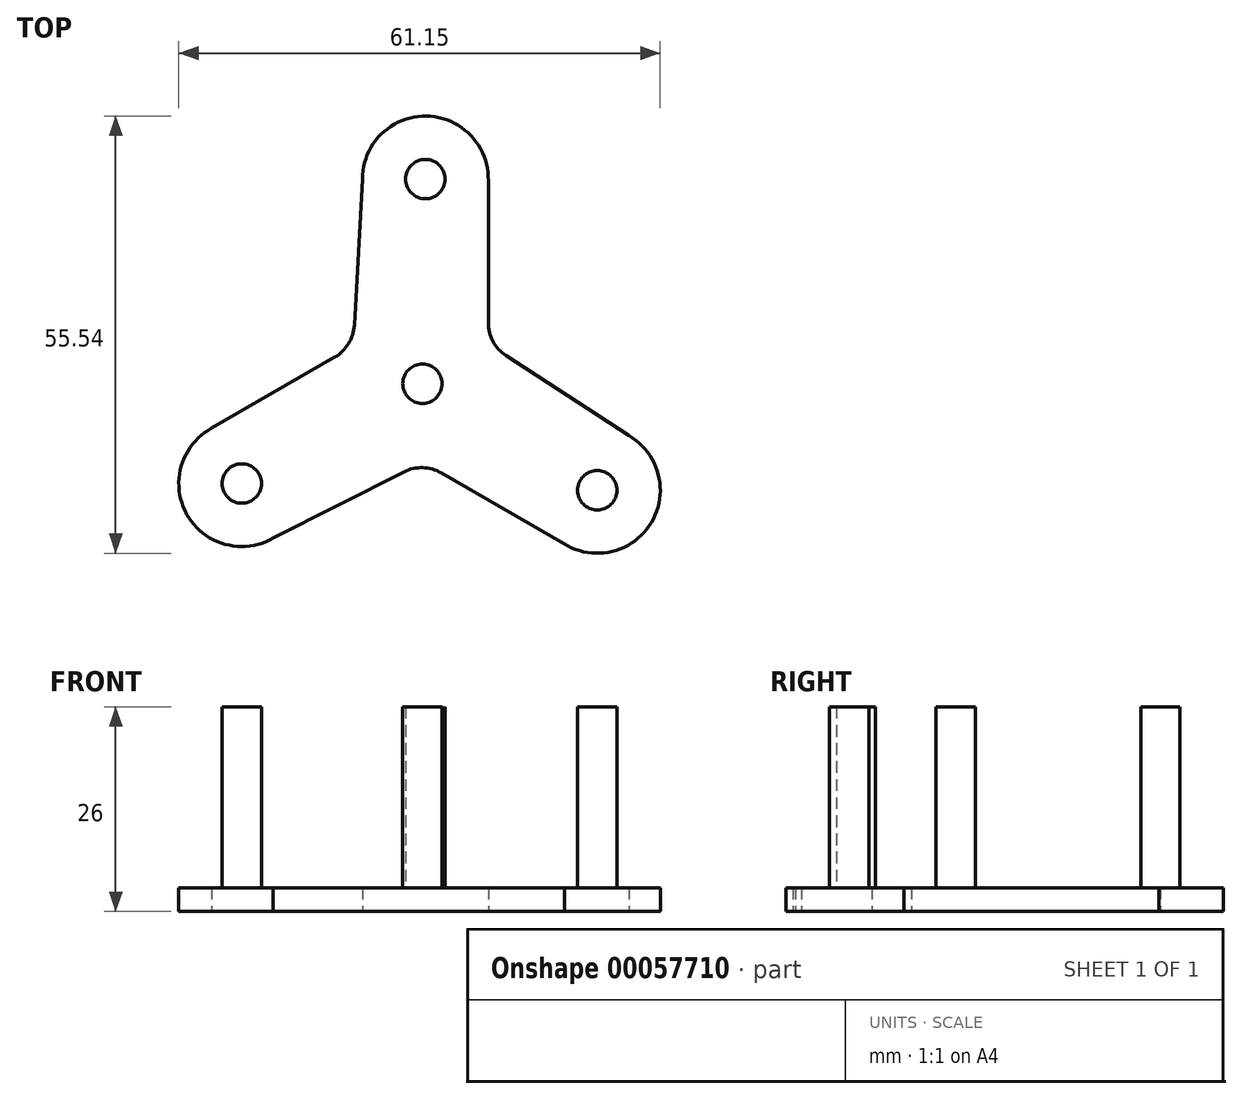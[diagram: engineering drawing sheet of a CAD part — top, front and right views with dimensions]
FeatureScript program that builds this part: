
annotation { "Feature Type Name" : "Feature", "Feature Type Description" : "" }
export const myFeature = defineFeature(function(context is Context, id is Id, definition is map)
    precondition{}
    {
        {
            var Q0;
            Q0=qCreatedBy(makeId("Top.planeOp"),FACE);
            var sketch = newSketch(context, id + "F0", { "sketchPlane" : qUnion([Q0])});
            skCircle(sketch, "E0", {"center": v(0, 0) * mm, "radius": 2.5 * mm});
            skCircle(sketch, "E1", {"center": v(0.37, 26) * mm, "radius": 2.5 * mm});
            skLineSegment(sketch, "E2", {"start": v(0.37, 26) * mm, "end": v(0, 0) * mm});
            skArc(sketch, "E3", {"start": v(8.37, 25.78) * mm, "mid": v(0.48, 34) * mm, "end": v(-7.63, 26) * mm});
            skCircle(sketch, "E4", {"center": v(0, 0) * mm, "radius": 9 * mm});
            skLineSegment(sketch, "E5", {"start": v(-8.65, 7.43) * mm, "end": v(-7.63, 26) * mm});
            skLineSegment(sketch, "E6", {"start": v(8.37, 25.78) * mm, "end": v(8.37, 7.75) * mm});
            skLineSegment(sketch, "E7.1.0", {"start": v(-2.36, -11.2) * mm, "end": v(-18.95, -19.6) * mm});
            skArc(sketch, "E7.1.1", {"start": v(-26.76, -5.65) * mm, "mid": v(-29.93, -16.59) * mm, "end": v(-18.95, -19.6) * mm});
            skLineSegment(sketch, "E7.1.2", {"start": v(-26.76, -5.65) * mm, "end": v(-11.15, 3.37) * mm});
            skCircle(sketch, "E7.1.3", {"center": v(-22.95, -12.68) * mm, "radius": 2.5 * mm});
            skLineSegment(sketch, "E7.1.4", {"start": v(-22.95, -12.68) * mm, "end": v(-0.25, 0) * mm});
            skLineSegment(sketch, "E7.2.0", {"start": v(10.63, 3.56) * mm, "end": v(26.2, -6.6) * mm});
            skArc(sketch, "E7.2.1", {"start": v(18.02, -20.35) * mm, "mid": v(29.08, -17.63) * mm, "end": v(26.2, -6.6) * mm});
            skLineSegment(sketch, "E7.2.2", {"start": v(18.02, -20.35) * mm, "end": v(2.4, -11.34) * mm});
            skCircle(sketch, "E7.2.3", {"center": v(22.2, -13.54) * mm, "radius": 2.5 * mm});
            skLineSegment(sketch, "E7.2.4", {"start": v(22.2, -13.54) * mm, "end": v(-0.13, -0.22) * mm});
            skPoint(sketch, "E7.center", {"position": v(-0.13, -0.07) * mm});
            skPoint(sketch, "E8.newPointA", {"position": v(-4.44, 7.24) * mm});
            skPoint(sketch, "E8.newPointB", {"position": v(-9.06, 0) * mm});
            skArc(sketch, "E8.filletArc", {"start": v(-11.15, 3.37) * mm, "mid": v(-9.39, 5.08) * mm, "end": v(-8.65, 7.43) * mm});
            skArc(sketch, "E9.1.0", {"start": v(2.4, -11.34) * mm, "mid": v(0.04, -10.67) * mm, "end": v(-2.36, -11.2) * mm});
            skArc(sketch, "E9.2.0", {"start": v(8.37, 7.75) * mm, "mid": v(8.97, 5.37) * mm, "end": v(10.63, 3.56) * mm});
            skPoint(sketch, "E10.orphan", {"position": v(8.37, 0) * mm});
            skPoint(sketch, "E11.orphan", {"position": v(4.4, 7.63) * mm});
            skPoint(sketch, "E12.orphan", {"position": v(4.28, -7.85) * mm});
            skSolve(sketch);
        }
        {
            var Q0;
            Q0 = qSketchRegion(id + "F0", true);
            var Q1;
            {var subQ0=sQuery(id+"F0.wireOp",EDGE,"E7.1.4");var subQ1=sQuery(id+"F0.wireOp",EDGE,"E0");var subQ2=makeQuery(id+"F0.imprint","INTERSECT",VERTEX,{"derivedFrom":[subQ1,subQ0]});Q1=makeQuery(id+"F0.imprint","IMPRINT",FACE,{"disambiguationData":[TD([[makeQuery(id+"F0.imprint","IMPRINT",EDGE,{"disambiguationData":[TD([[subQ2,-1.0]])],"derivedFrom":subQ1}),-1.0]])]});}
            var Q2;
            {var subQ0=sQuery(id+"F0.wireOp",EDGE,"E7.1.4");var subQ1=sQuery(id+"F0.wireOp",EDGE,"E0");var subQ2=makeQuery(id+"F0.imprint","INTERSECT",VERTEX,{"derivedFrom":[subQ1,subQ0]});Q2=makeQuery(id+"F0.imprint","IMPRINT",FACE,{"disambiguationData":[TD([[makeQuery(id+"F0.imprint","IMPRINT",EDGE,{"disambiguationData":[TD([[subQ2,1.0]])],"derivedFrom":subQ1}),-1.0]])]});}
            var Q3;
            {var subQ0=sQuery(id+"F0.wireOp",EDGE,"E2");var subQ1=sQuery(id+"F0.wireOp",EDGE,"E0");var subQ2=makeQuery(id+"F0.imprint","INTERSECT",VERTEX,{"derivedFrom":[subQ1,subQ0]});Q3=makeQuery(id+"F0.imprint","IMPRINT",FACE,{"disambiguationData":[TD([[makeQuery(id+"F0.imprint","IMPRINT",EDGE,{"disambiguationData":[TD([[subQ2,1.0]])],"derivedFrom":subQ1}),-1.0]])]});}
            var Q4;
            Q4=makeQuery(id+"F0.imprint","IMPRINT",FACE,{"disambiguationData":[TD([[makeQuery(id+"F0.imprint","IMPRINT",EDGE,{"derivedFrom":sQuery(id+"F0.wireOp",EDGE,"E1")}),1.0]])]});
            var Q5;
            Q5=makeQuery(id+"F0.imprint","IMPRINT",FACE,{"disambiguationData":[TD([[makeQuery(id+"F0.imprint","IMPRINT",EDGE,{"derivedFrom":sQuery(id+"F0.wireOp",EDGE,"E7.2.3")}),1.0]])]});
            var Q6;
            {var subQ0=sQuery(id+"F0.wireOp",EDGE,"E0");var subQ1=makeQuery(id+"F0.imprint","INTERSECT",VERTEX,{"derivedFrom":[subQ0,sQuery(id+"F0.wireOp",EDGE,"E7.1.4")]});Q6=makeQuery(id+"F0.imprint","IMPRINT",FACE,{"disambiguationData":[TD([[makeQuery(id+"F0.imprint","IMPRINT",EDGE,{"disambiguationData":[TD([[subQ1,1.0]])],"derivedFrom":subQ0}),1.0]])]});}
            var Q7;
            Q7=makeQuery(id+"F0.imprint","IMPRINT",FACE,{"disambiguationData":[TD([[makeQuery(id+"F0.imprint","IMPRINT",EDGE,{"derivedFrom":sQuery(id+"F0.wireOp",EDGE,"E7.1.3")}),1.0]])]});
            extrude(context, id + "F1", {"entities" : qUnion([Q0, Q1, Q2, Q3, Q4, Q5, Q6, Q7]), "depth" : 3 * mm});
        }
        {
            var Q0;
            Q0=makeQuery(id+"F1.opExtrude","CAP_FACE",FACE,{"disambiguationData":[OSD([sQuery(id+"F0.wireOp",EDGE,"E3"),sQuery(id+"F0.wireOp",EDGE,"E5"),sQuery(id+"F0.wireOp",EDGE,"E6"),sQuery(id+"F0.wireOp",EDGE,"E7.1.0"),sQuery(id+"F0.wireOp",EDGE,"E7.1.1"),sQuery(id+"F0.wireOp",EDGE,"E7.1.2"),sQuery(id+"F0.wireOp",EDGE,"E7.2.0"),sQuery(id+"F0.wireOp",EDGE,"E7.2.1"),sQuery(id+"F0.wireOp",EDGE,"E7.2.2"),sQuery(id+"F0.wireOp",EDGE,"E8.filletArc"),sQuery(id+"F0.wireOp",EDGE,"E9.1.0"),sQuery(id+"F0.wireOp",EDGE,"E9.2.0")])],"isStart":false});
            var sketch = newSketch(context, id + "F2", { "sketchPlane" : qUnion([Q0])});
            skCircle(sketch, "E13", {"center": v(-22.95, -12.68) * mm, "radius": 8 * mm});
            skPoint(sketch, "E13.first.point", {"position": v(-29.58, -8.2) * mm});
            skPoint(sketch, "E13.second.point", {"position": v(-29.93, -16.59) * mm});
            skPoint(sketch, "E13.third.point", {"position": v(-22.27, -20.65) * mm});
            skCircle(sketch, "E14", {"center": v(0.37, 26) * mm, "radius": 8 * mm});
            skPoint(sketch, "E14.first.point", {"position": v(-6.8, 29.55) * mm});
            skPoint(sketch, "E14.second.point", {"position": v(0, 33.99) * mm});
            skPoint(sketch, "E14.third.point", {"position": v(7.37, 29.86) * mm});
            skCircle(sketch, "E15", {"center": v(22.2, -13.54) * mm, "radius": 8 * mm});
            skPoint(sketch, "E15.first.point", {"position": v(23.54, -21.42) * mm});
            skPoint(sketch, "E15.second.point", {"position": v(29.08, -17.63) * mm});
            skPoint(sketch, "E15.third.point", {"position": v(29.08, -9.44) * mm});
            skPoint(sketch, "E15.third.point.positionSnap0", {"position": v(29.08, -17.63) * mm});
            skCircle(sketch, "E16", {"center": v(0.37, 26) * mm, "radius": 2.5 * mm});
            skCircle(sketch, "E17", {"center": v(-22.95, -12.68) * mm, "radius": 2.5 * mm});
            skCircle(sketch, "E18", {"center": v(22.2, -13.54) * mm, "radius": 2.5 * mm});
            skCircle(sketch, "E19", {"center": v(0, 0) * mm, "radius": 2.5 * mm});
            skSolve(sketch);
        }
        {
            var Q0;
            Q0=makeQuery(id+"F2.imprint","IMPRINT",FACE,{"disambiguationData":[TD([[makeQuery(id+"F2.imprint","IMPRINT",EDGE,{"derivedFrom":sQuery(id+"F2.wireOp",EDGE,"E17")}),1.0]])]});
            var Q1;
            Q1=makeQuery(id+"F2.imprint","IMPRINT",FACE,{"disambiguationData":[TD([[makeQuery(id+"F2.imprint","IMPRINT",EDGE,{"derivedFrom":sQuery(id+"F2.wireOp",EDGE,"E16")}),1.0]])]});
            var Q2;
            Q2=makeQuery(id+"F2.imprint","IMPRINT",FACE,{"disambiguationData":[TD([[makeQuery(id+"F2.imprint","IMPRINT",EDGE,{"derivedFrom":sQuery(id+"F2.wireOp",EDGE,"E18")}),1.0]])]});
            var Q3;
            Q3=makeQuery(id+"F2.imprint","IMPRINT",FACE,{"disambiguationData":[TD([[makeQuery(id+"F2.imprint","IMPRINT",EDGE,{"derivedFrom":sQuery(id+"F2.wireOp",EDGE,"E19")}),1.0]])]});
            extrude(context, id + "F3", {"entities" : qUnion([Q0, Q1, Q2, Q3]), "operationType" : NewBodyOperationType.ADD, "depth" : 23 * mm});
        }
    });
